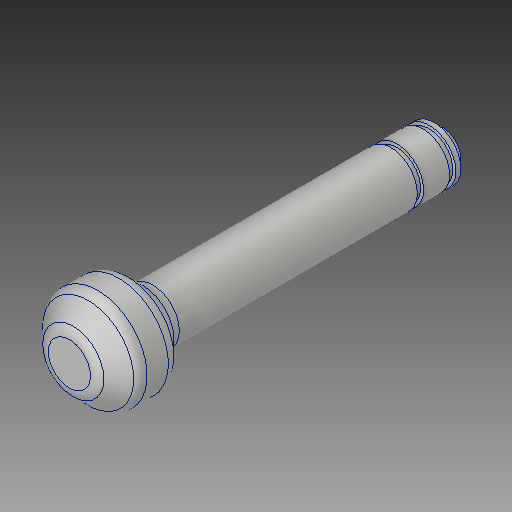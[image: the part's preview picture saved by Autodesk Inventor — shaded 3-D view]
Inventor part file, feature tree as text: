
AUTODESK INVENTOR PART (.ipt)
format: ipt  version: 2017 (Build 210142000, 142)  size: 135,168 bytes
history: native  units: in
note: dims shown in document units (in); Inventor stores cm internally (conversion verified against a paired STEP export)
features: chamfer x1
ambient origin geometry x8: Origin, YZ Plane, XZ Plane, XY Plane, X Axis, Y Axis, Z Axis, Center Point
bodies: Solid1 (feature_tree)
feature tree (1):
  chamfer  "Chamfer1"  [1 undecoded]
note: 1 required parameter value undecoded (feature->parameter linkage not recoverable at this tier; creation-order binding heuristic only, values carry confidence <= 0.55)
